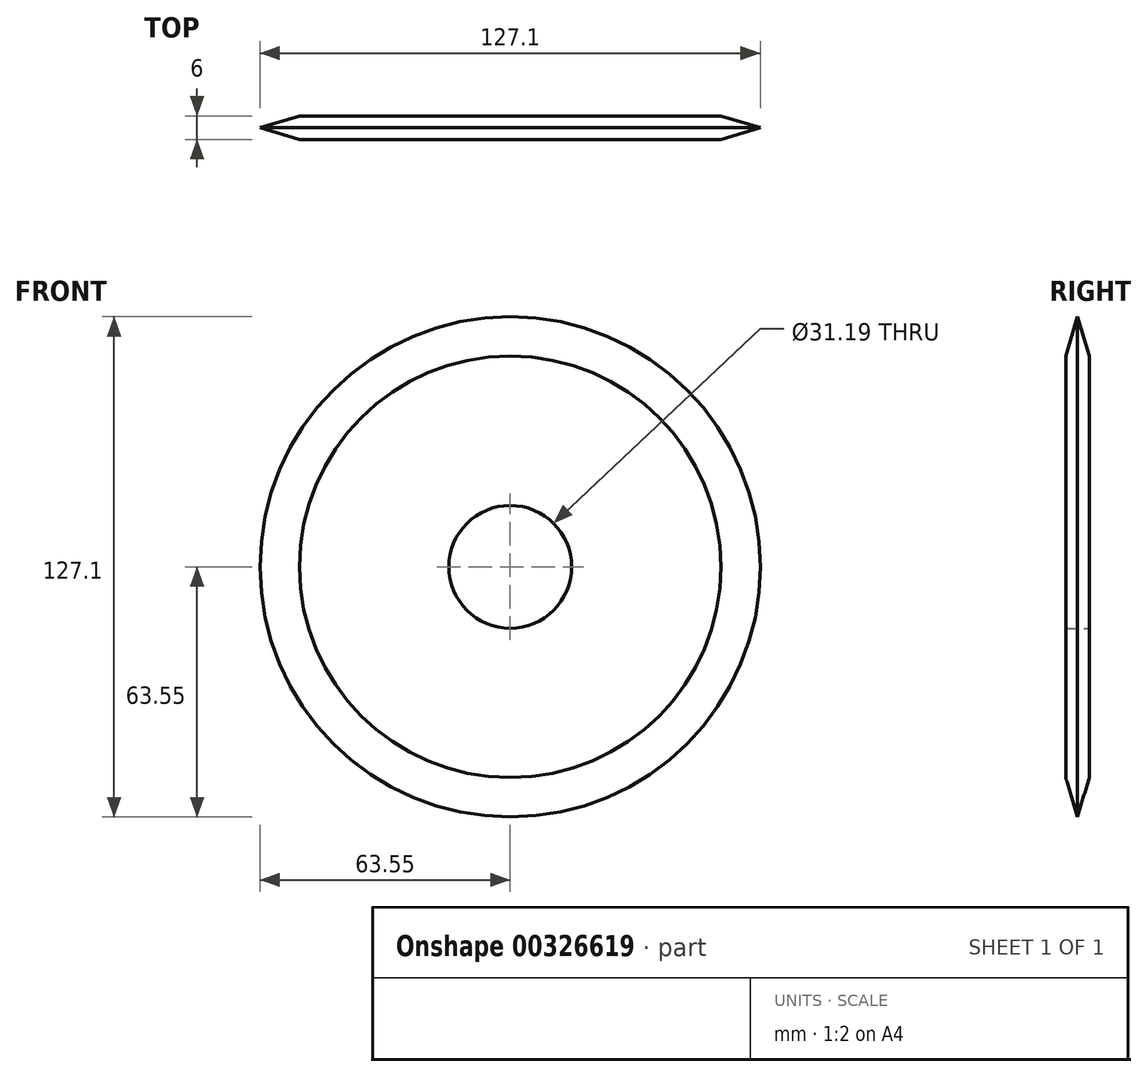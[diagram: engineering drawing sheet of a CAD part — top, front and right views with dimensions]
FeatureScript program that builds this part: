
annotation { "Feature Type Name" : "Feature", "Feature Type Description" : "" }
export const myFeature = defineFeature(function(context is Context, id is Id, definition is map)
    precondition{}
    {
        {
            var Q0;
            Q0=qCreatedBy(makeId("Front.planeOp"),FACE);
            var sketch = newSketch(context, id + "F0", { "sketchPlane" : qUnion([Q0])});
            skCircle(sketch, "E0", {"center": v(0, 0) * mm, "radius": 63.55 * mm});
            skCircle(sketch, "E1", {"center": v(0, 0) * mm, "radius": 15.6 * mm});
            skSolve(sketch);
        }
        {
            var Q0;
            Q0 = qSketchRegion(id + "F0", true);
            extrude(context, id + "F1", {"entities" : qUnion([Q0]), "endBound" : BoundingType.SYMMETRIC, "depth" : 6 * mm});
        }
        {
            var Q0;
            Q0=makeQuery(id+"F1.opExtrude","CAP_EDGE",EDGE,{"disambiguationData":[OSD([sQuery(id+"F0.wireOp",EDGE,"E0")])],"isStart":false});
            var Q1;
            Q1=makeQuery(id+"F1.opExtrude","CAP_EDGE",EDGE,{"disambiguationData":[OSD([sQuery(id+"F0.wireOp",EDGE,"E0")])],"isStart":true});
            chamfer(context, id + "F2", {"entities" : qUnion([Q0, Q1]), "chamferType" : ChamferType.TWO_OFFSETS, "width1" : 3 * mm, "oppositeDirection" : true, "width2" : 10 * mm, "tangentPropagation" : true});
        }
    });
